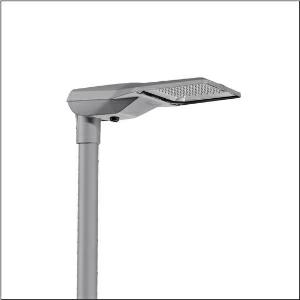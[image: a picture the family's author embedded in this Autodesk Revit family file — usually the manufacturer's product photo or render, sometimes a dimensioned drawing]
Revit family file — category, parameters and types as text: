
# Revit family: streetlight_sl_21_iq_midi___st1_0a_5xe3d31u08nb_218c
name_source: partatom
category: Lighting Fixtures
units: mm (PartAtom-declared; Revit-internal decimal feet)

## family parameters
Cut with Voids When Loaded = No
Host = Face
Light Source = No
Part Type = Normal
Room Calculation Point = No
Round Connector Dimension = Use Diameter
Shared = No

## types (1)
- --- (1 x LED, 21550 lm, 136.6 W, 3000K)
    Apparent Load = 137 VA
    CIE Flux Codes = 40 73 97 100 100
    Color Rendering = 70
    Color Temperature = 3000K
    Default Elevation = 1800 mm
    Description = Streetlight SL 21 iQ midi, mast luminaire, primary light control with lens, of PMMA, primary optical cover: cover, of toughened safety glass, transparent, light distribution: ST1.0a, light emission: direct distribution, primary light characteristic: asymmetric, installation type: post-top, side-entry, LED, High Power LED, rated luminous flux: 21.550lm, luminous efficacy: 158lm/W, light colour: 730, colour temperature: 3000K, control: presetting dimming logarithmic, Street-Remote, Auto-Match, Temp-Guard, Lumen-Switch, Night-Set, Smart-Wire, Light-Fading, Desk-Remote (wireless, voltage-free reading and setting of iQ features in the workshop via application-optimized NFC function/RFID function), optimised constant luminous flux control (CLO 2.0), mains connection: 230..240V, AC, 50/60Hz, start of lifetime: 137W, end of service life: 144W, reduction: 61W, luminaire housing, of diecast aluminium, powder-coated, Siteco® metallic grey (DB 702S), corrosivity category C5 mid according to DIN EN ISO 12944, please order mast flange separately, inclination adjustable: 0°, 5°, 10°, 15°, sealing non-destructively replaceable, multi-level sealing system, length: 644mm, width: 335mm, height: 110mm, mast flange for spigot size: 42mm (side-entry): 5XC10008XM4, 60/48mm (side-entry/post-top): 5XC10108XM2, 76/60mm (side-entry/post-top): 5XC10108XM1, Smart Interface below, protection rating (complete): IP66, insulation class (complete): insulation class II (safety insulation), certification: CE, ENEC, ENEC+, VDE, impact resistance: IK09, permissible operating ambient temperature for outdoor applications: -40..+50°C, standard-compliant lighting for roads and squares, packaging unit: 1 piece

Light Distribution: ST1.0a
    Height = 111 mm
    Lamp = 1 x LED
    Lamp Light Flux = 21550 lm
    Lamp Power = 136.6 W
    Lamp count = 1
    Length = 644 mm
    Luminous efficacy = 158 lm/W
    Manufacturer = Siteco
    ModVariant = No
    Model = 5XE3D31U08NB
    Number of Poles = 1
    OnlyDefault = Yes
    Power Factor = 1
    Product Name = Streetlight SL 21 iQ midi | ST1.0a
    Product group = mast luminaire | pylon top
    ProductGroupID = 6100
    Protection Class = Protection class II
    Protection Degree = IP 66
    RLX_Detail_Level = 1
    RLX_Emergency_Light_Flux = 0 lm
    RLX_Emergency_Type = 0
    RLX_Emergency_Type_DB = No
    RlxData = <blob elided: 91101 chars, md5=a7a7bdca>
    Socket = socket
    Standby Power = 0 W
    System Light Flux = 21550 lm
    System Power = 137 W
    Type Comments = factory setting: luminous flux: 100 % | dim-lin: 254 | 733 mA
    Type Image = l_1004300.jpg
    URL = http://relux.com
    VarID = @adj_043997
    Voltage = 0 V
    Weight = 0.00 kg
    Width = 336 mm

## geometry (parser evidence)
native form markers: Blend x4, Sweep x10
no freeform markers — native parametric forms only
